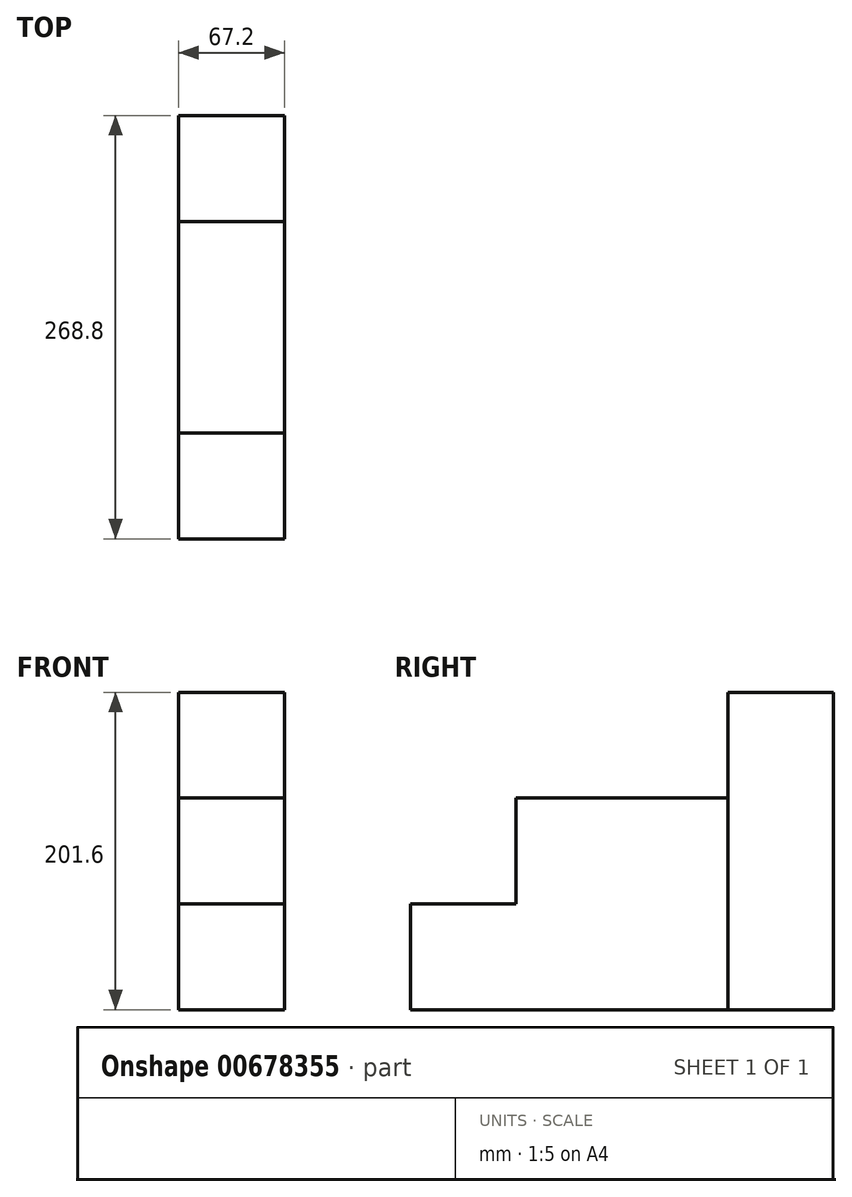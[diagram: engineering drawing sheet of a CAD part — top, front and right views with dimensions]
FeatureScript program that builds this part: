
annotation { "Feature Type Name" : "Feature", "Feature Type Description" : "" }
export const myFeature = defineFeature(function(context is Context, id is Id, definition is map)
    precondition{}
    {
        {
            var Q0;
            Q0=qCreatedBy(makeId("Top.planeOp"),FACE);
            var sketch = newSketch(context, id + "F0", { "sketchPlane" : qUnion([Q0])});
            skLineSegment(sketch, "E0", {"start": v(0, 0) * mm, "end": v(67.2, 0) * mm});
            skLineSegment(sketch, "E1", {"start": v(67.2, 0) * mm, "end": v(67.2, 67.2) * mm});
            skLineSegment(sketch, "E2", {"start": v(67.2, 67.2) * mm, "end": v(0, 67.2) * mm});
            skLineSegment(sketch, "E3", {"start": v(0, 67.2) * mm, "end": v(0, 0) * mm});
            skLineSegment(sketch, "E4.0.1.0", {"start": v(0, 134.4) * mm, "end": v(0, 67.2) * mm});
            skLineSegment(sketch, "E4.0.1.1", {"start": v(0, 67.2) * mm, "end": v(67.2, 67.2) * mm});
            skLineSegment(sketch, "E4.0.1.2", {"start": v(67.2, 67.2) * mm, "end": v(67.2, 134.4) * mm});
            skLineSegment(sketch, "E4.0.1.3", {"start": v(67.2, 134.4) * mm, "end": v(0, 134.4) * mm});
            skLineSegment(sketch, "E4.0.2.0", {"start": v(0, 201.6) * mm, "end": v(0, 134.4) * mm});
            skLineSegment(sketch, "E4.0.2.1", {"start": v(0, 134.4) * mm, "end": v(67.2, 134.4) * mm});
            skLineSegment(sketch, "E4.0.2.2", {"start": v(67.2, 134.4) * mm, "end": v(67.2, 201.6) * mm});
            skLineSegment(sketch, "E4.0.2.3", {"start": v(67.2, 201.6) * mm, "end": v(0, 201.6) * mm});
            skLineSegment(sketch, "E4.0.3.0", {"start": v(0, 268.8) * mm, "end": v(0, 201.6) * mm});
            skLineSegment(sketch, "E4.0.3.1", {"start": v(0, 201.6) * mm, "end": v(67.2, 201.6) * mm});
            skLineSegment(sketch, "E4.0.3.2", {"start": v(67.2, 201.6) * mm, "end": v(67.2, 268.8) * mm});
            skLineSegment(sketch, "E4.0.3.3", {"start": v(67.2, 268.8) * mm, "end": v(0, 268.8) * mm});
            skLineSegment(sketch, "E4.0.4.0", {"start": v(0, 336) * mm, "end": v(0, 268.8) * mm});
            skLineSegment(sketch, "E4.0.4.1", {"start": v(0, 268.8) * mm, "end": v(67.2, 268.8) * mm});
            skLineSegment(sketch, "E4.0.4.2", {"start": v(67.2, 268.8) * mm, "end": v(67.2, 336) * mm});
            skLineSegment(sketch, "E4.0.4.3", {"start": v(67.2, 336) * mm, "end": v(0, 336) * mm});
            skLineSegment(sketch, "E4.1.0.0", {"start": v(67.2, 67.2) * mm, "end": v(67.2, 0) * mm});
            skLineSegment(sketch, "E4.1.0.1", {"start": v(67.2, 0) * mm, "end": v(134.4, 0) * mm});
            skLineSegment(sketch, "E4.1.0.2", {"start": v(134.4, 0) * mm, "end": v(134.4, 67.2) * mm});
            skLineSegment(sketch, "E4.1.0.3", {"start": v(134.4, 67.2) * mm, "end": v(67.2, 67.2) * mm});
            skLineSegment(sketch, "E4.1.1.0", {"start": v(67.2, 134.4) * mm, "end": v(67.2, 67.2) * mm});
            skLineSegment(sketch, "E4.1.1.1", {"start": v(67.2, 67.2) * mm, "end": v(134.4, 67.2) * mm});
            skLineSegment(sketch, "E4.1.1.2", {"start": v(134.4, 67.2) * mm, "end": v(134.4, 134.4) * mm});
            skLineSegment(sketch, "E4.1.1.3", {"start": v(134.4, 134.4) * mm, "end": v(67.2, 134.4) * mm});
            skLineSegment(sketch, "E4.1.2.0", {"start": v(67.2, 201.6) * mm, "end": v(67.2, 134.4) * mm});
            skLineSegment(sketch, "E4.1.2.1", {"start": v(67.2, 134.4) * mm, "end": v(134.4, 134.4) * mm});
            skLineSegment(sketch, "E4.1.2.2", {"start": v(134.4, 134.4) * mm, "end": v(134.4, 201.6) * mm});
            skLineSegment(sketch, "E4.1.2.3", {"start": v(134.4, 201.6) * mm, "end": v(67.2, 201.6) * mm});
            skLineSegment(sketch, "E4.1.3.0", {"start": v(67.2, 268.8) * mm, "end": v(67.2, 201.6) * mm});
            skLineSegment(sketch, "E4.1.3.1", {"start": v(67.2, 201.6) * mm, "end": v(134.4, 201.6) * mm});
            skLineSegment(sketch, "E4.1.3.2", {"start": v(134.4, 201.6) * mm, "end": v(134.4, 268.8) * mm});
            skLineSegment(sketch, "E4.1.3.3", {"start": v(134.4, 268.8) * mm, "end": v(67.2, 268.8) * mm});
            skLineSegment(sketch, "E4.1.4.0", {"start": v(67.2, 336) * mm, "end": v(67.2, 268.8) * mm});
            skLineSegment(sketch, "E4.1.4.1", {"start": v(67.2, 268.8) * mm, "end": v(134.4, 268.8) * mm});
            skLineSegment(sketch, "E4.1.4.2", {"start": v(134.4, 268.8) * mm, "end": v(134.4, 336) * mm});
            skLineSegment(sketch, "E4.1.4.3", {"start": v(134.4, 336) * mm, "end": v(67.2, 336) * mm});
            skLineSegment(sketch, "E4.2.0.0", {"start": v(134.4, 67.2) * mm, "end": v(134.4, 0) * mm});
            skLineSegment(sketch, "E4.2.0.1", {"start": v(134.4, 0) * mm, "end": v(201.6, 0) * mm});
            skLineSegment(sketch, "E4.2.0.2", {"start": v(201.6, 0) * mm, "end": v(201.6, 67.2) * mm});
            skLineSegment(sketch, "E4.2.0.3", {"start": v(201.6, 67.2) * mm, "end": v(134.4, 67.2) * mm});
            skLineSegment(sketch, "E4.2.1.0", {"start": v(134.4, 134.4) * mm, "end": v(134.4, 67.2) * mm});
            skLineSegment(sketch, "E4.2.1.1", {"start": v(134.4, 67.2) * mm, "end": v(201.6, 67.2) * mm});
            skLineSegment(sketch, "E4.2.1.2", {"start": v(201.6, 67.2) * mm, "end": v(201.6, 134.4) * mm});
            skLineSegment(sketch, "E4.2.1.3", {"start": v(201.6, 134.4) * mm, "end": v(134.4, 134.4) * mm});
            skLineSegment(sketch, "E4.2.2.0", {"start": v(134.4, 201.6) * mm, "end": v(134.4, 134.4) * mm});
            skLineSegment(sketch, "E4.2.2.1", {"start": v(134.4, 134.4) * mm, "end": v(201.6, 134.4) * mm});
            skLineSegment(sketch, "E4.2.2.2", {"start": v(201.6, 134.4) * mm, "end": v(201.6, 201.6) * mm});
            skLineSegment(sketch, "E4.2.2.3", {"start": v(201.6, 201.6) * mm, "end": v(134.4, 201.6) * mm});
            skLineSegment(sketch, "E4.2.3.0", {"start": v(134.4, 268.8) * mm, "end": v(134.4, 201.6) * mm});
            skLineSegment(sketch, "E4.2.3.1", {"start": v(134.4, 201.6) * mm, "end": v(201.6, 201.6) * mm});
            skLineSegment(sketch, "E4.2.3.2", {"start": v(201.6, 201.6) * mm, "end": v(201.6, 268.8) * mm});
            skLineSegment(sketch, "E4.2.3.3", {"start": v(201.6, 268.8) * mm, "end": v(134.4, 268.8) * mm});
            skLineSegment(sketch, "E4.2.4.0", {"start": v(134.4, 336) * mm, "end": v(134.4, 268.8) * mm});
            skLineSegment(sketch, "E4.2.4.1", {"start": v(134.4, 268.8) * mm, "end": v(201.6, 268.8) * mm});
            skLineSegment(sketch, "E4.2.4.2", {"start": v(201.6, 268.8) * mm, "end": v(201.6, 336) * mm});
            skLineSegment(sketch, "E4.2.4.3", {"start": v(201.6, 336) * mm, "end": v(134.4, 336) * mm});
            skLineSegment(sketch, "E4.3.0.0", {"start": v(201.6, 67.2) * mm, "end": v(201.6, 0) * mm});
            skLineSegment(sketch, "E4.3.0.1", {"start": v(201.6, 0) * mm, "end": v(268.8, 0) * mm});
            skLineSegment(sketch, "E4.3.0.2", {"start": v(268.8, 0) * mm, "end": v(268.8, 67.2) * mm});
            skLineSegment(sketch, "E4.3.0.3", {"start": v(268.8, 67.2) * mm, "end": v(201.6, 67.2) * mm});
            skLineSegment(sketch, "E4.3.1.0", {"start": v(201.6, 134.4) * mm, "end": v(201.6, 67.2) * mm});
            skLineSegment(sketch, "E4.3.1.1", {"start": v(201.6, 67.2) * mm, "end": v(268.8, 67.2) * mm});
            skLineSegment(sketch, "E4.3.1.2", {"start": v(268.8, 67.2) * mm, "end": v(268.8, 134.4) * mm});
            skLineSegment(sketch, "E4.3.1.3", {"start": v(268.8, 134.4) * mm, "end": v(201.6, 134.4) * mm});
            skLineSegment(sketch, "E4.3.2.0", {"start": v(201.6, 201.6) * mm, "end": v(201.6, 134.4) * mm});
            skLineSegment(sketch, "E4.3.2.1", {"start": v(201.6, 134.4) * mm, "end": v(268.8, 134.4) * mm});
            skLineSegment(sketch, "E4.3.2.2", {"start": v(268.8, 134.4) * mm, "end": v(268.8, 201.6) * mm});
            skLineSegment(sketch, "E4.3.2.3", {"start": v(268.8, 201.6) * mm, "end": v(201.6, 201.6) * mm});
            skLineSegment(sketch, "E4.3.3.0", {"start": v(201.6, 268.8) * mm, "end": v(201.6, 201.6) * mm});
            skLineSegment(sketch, "E4.3.3.1", {"start": v(201.6, 201.6) * mm, "end": v(268.8, 201.6) * mm});
            skLineSegment(sketch, "E4.3.3.2", {"start": v(268.8, 201.6) * mm, "end": v(268.8, 268.8) * mm});
            skLineSegment(sketch, "E4.3.3.3", {"start": v(268.8, 268.8) * mm, "end": v(201.6, 268.8) * mm});
            skLineSegment(sketch, "E4.3.4.0", {"start": v(201.6, 336) * mm, "end": v(201.6, 268.8) * mm});
            skLineSegment(sketch, "E4.3.4.1", {"start": v(201.6, 268.8) * mm, "end": v(268.8, 268.8) * mm});
            skLineSegment(sketch, "E4.3.4.2", {"start": v(268.8, 268.8) * mm, "end": v(268.8, 336) * mm});
            skLineSegment(sketch, "E4.3.4.3", {"start": v(268.8, 336) * mm, "end": v(201.6, 336) * mm});
            skLineSegment(sketch, "E4.4.0.0", {"start": v(268.8, 67.2) * mm, "end": v(268.8, 0) * mm});
            skLineSegment(sketch, "E4.4.0.1", {"start": v(268.8, 0) * mm, "end": v(336, 0) * mm});
            skLineSegment(sketch, "E4.4.0.2", {"start": v(336, 0) * mm, "end": v(336, 67.2) * mm});
            skLineSegment(sketch, "E4.4.0.3", {"start": v(336, 67.2) * mm, "end": v(268.8, 67.2) * mm});
            skLineSegment(sketch, "E4.4.1.0", {"start": v(268.8, 134.4) * mm, "end": v(268.8, 67.2) * mm});
            skLineSegment(sketch, "E4.4.1.1", {"start": v(268.8, 67.2) * mm, "end": v(336, 67.2) * mm});
            skLineSegment(sketch, "E4.4.1.2", {"start": v(336, 67.2) * mm, "end": v(336, 134.4) * mm});
            skLineSegment(sketch, "E4.4.1.3", {"start": v(336, 134.4) * mm, "end": v(268.8, 134.4) * mm});
            skLineSegment(sketch, "E4.4.2.0", {"start": v(268.8, 201.6) * mm, "end": v(268.8, 134.4) * mm});
            skLineSegment(sketch, "E4.4.2.1", {"start": v(268.8, 134.4) * mm, "end": v(336, 134.4) * mm});
            skLineSegment(sketch, "E4.4.2.2", {"start": v(336, 134.4) * mm, "end": v(336, 201.6) * mm});
            skLineSegment(sketch, "E4.4.2.3", {"start": v(336, 201.6) * mm, "end": v(268.8, 201.6) * mm});
            skLineSegment(sketch, "E4.4.3.0", {"start": v(268.8, 268.8) * mm, "end": v(268.8, 201.6) * mm});
            skLineSegment(sketch, "E4.4.3.1", {"start": v(268.8, 201.6) * mm, "end": v(336, 201.6) * mm});
            skLineSegment(sketch, "E4.4.3.2", {"start": v(336, 201.6) * mm, "end": v(336, 268.8) * mm});
            skLineSegment(sketch, "E4.4.3.3", {"start": v(336, 268.8) * mm, "end": v(268.8, 268.8) * mm});
            skLineSegment(sketch, "E4.4.4.0", {"start": v(268.8, 336) * mm, "end": v(268.8, 268.8) * mm});
            skLineSegment(sketch, "E4.4.4.1", {"start": v(268.8, 268.8) * mm, "end": v(336, 268.8) * mm});
            skLineSegment(sketch, "E4.4.4.2", {"start": v(336, 268.8) * mm, "end": v(336, 336) * mm});
            skLineSegment(sketch, "E4.4.4.3", {"start": v(336, 336) * mm, "end": v(268.8, 336) * mm});
            skLineSegment(sketch, "E4.direction1", {"start": v(0, 0) * mm, "end": v(67.2, 0) * mm, "construction": true});
            skLineSegment(sketch, "E4.direction2", {"start": v(0, 0) * mm, "end": v(0, 67.2) * mm, "construction": true});
            skSolve(sketch);
        }
        {
            var Q0;
            Q0=makeQuery(id+"F0.imprint","IMPRINT",FACE,{"disambiguationData":[TD([[makeQuery(id+"F0.imprint","IMPRINT",EDGE,{"derivedFrom":sQuery(id+"F0.wireOp",EDGE,"E4.0.4.0")}),1.0]])]});
            var Q1;
            Q1=makeQuery(id+"F0.imprint","IMPRINT",FACE,{"disambiguationData":[TD([[makeQuery(id+"F0.imprint","IMPRINT",EDGE,{"derivedFrom":sQuery(id+"F0.wireOp",EDGE,"E4.4.4.0")}),1.0]])]});
            var Q2;
            Q2=makeQuery(id+"F0.imprint","IMPRINT",FACE,{"disambiguationData":[TD([[makeQuery(id+"F0.imprint","IMPRINT",EDGE,{"derivedFrom":sQuery(id+"F0.wireOp",EDGE,"E4.4.3.0")}),1.0]])]});
            var Q3;
            Q3=makeQuery(id+"F0.imprint","IMPRINT",FACE,{"disambiguationData":[TD([[makeQuery(id+"F0.imprint","IMPRINT",EDGE,{"derivedFrom":sQuery(id+"F0.wireOp",EDGE,"E4.1.4.0")}),1.0]])]});
            var Q4;
            Q4=makeQuery(id+"F0.imprint","IMPRINT",FACE,{"disambiguationData":[TD([[makeQuery(id+"F0.imprint","IMPRINT",EDGE,{"derivedFrom":sQuery(id+"F0.wireOp",EDGE,"E4.3.4.0")}),1.0]])]});
            extrude(context, id + "F1", {"entities" : qUnion([Q0, Q1, Q2, Q3, Q4]), "depth" : (336 * 3 / 5) * mm, "offsetDistance" : 25 * mm});
        }
        {
            var Q0;
            Q0=makeQuery(id+"F0.imprint","IMPRINT",FACE,{"disambiguationData":[TD([[makeQuery(id+"F0.imprint","IMPRINT",EDGE,{"derivedFrom":sQuery(id+"F0.wireOp",EDGE,"E4.0.3.0")}),1.0]])]});
            var Q1;
            Q1=makeQuery(id+"F0.imprint","IMPRINT",FACE,{"disambiguationData":[TD([[makeQuery(id+"F0.imprint","IMPRINT",EDGE,{"derivedFrom":sQuery(id+"F0.wireOp",EDGE,"E4.0.2.0")}),1.0]])]});
            var Q2;
            Q2=makeQuery(id+"F0.imprint","IMPRINT",FACE,{"disambiguationData":[TD([[makeQuery(id+"F0.imprint","IMPRINT",EDGE,{"derivedFrom":sQuery(id+"F0.wireOp",EDGE,"E4.3.3.0")}),1.0]])]});
            var Q3;
            Q3=makeQuery(id+"F0.imprint","IMPRINT",FACE,{"disambiguationData":[TD([[makeQuery(id+"F0.imprint","IMPRINT",EDGE,{"derivedFrom":sQuery(id+"F0.wireOp",EDGE,"E4.4.2.0")}),1.0]])]});
            var Q4;
            Q4=makeQuery(id+"F0.imprint","IMPRINT",FACE,{"disambiguationData":[TD([[makeQuery(id+"F0.imprint","IMPRINT",EDGE,{"derivedFrom":sQuery(id+"F0.wireOp",EDGE,"E4.2.4.0")}),1.0]])]});
            extrude(context, id + "F2", {"entities" : qUnion([Q0, Q1, Q2, Q3, Q4]), "depth" : (336 * 2 / 5) * mm, "offsetDistance" : 25 * mm});
        }
        {
            var Q0;
            Q0=makeQuery(id+"F0.imprint","IMPRINT",FACE,{"disambiguationData":[TD([[makeQuery(id+"F0.imprint","IMPRINT",EDGE,{"derivedFrom":sQuery(id+"F0.wireOp",EDGE,"E4.1.2.0")}),1.0]])]});
            var Q1;
            Q1=makeQuery(id+"F0.imprint","IMPRINT",FACE,{"disambiguationData":[TD([[makeQuery(id+"F0.imprint","IMPRINT",EDGE,{"derivedFrom":sQuery(id+"F0.wireOp",EDGE,"E4.0.1.0")}),1.0]])]});
            var Q2;
            Q2=makeQuery(id+"F0.imprint","IMPRINT",FACE,{"disambiguationData":[TD([[makeQuery(id+"F0.imprint","IMPRINT",EDGE,{"derivedFrom":sQuery(id+"F0.wireOp",EDGE,"E4.3.1.0")}),1.0]])]});
            var Q3;
            Q3=makeQuery(id+"F0.imprint","IMPRINT",FACE,{"disambiguationData":[TD([[makeQuery(id+"F0.imprint","IMPRINT",EDGE,{"derivedFrom":sQuery(id+"F0.wireOp",EDGE,"E4.4.1.0")}),1.0]])]});
            var Q4;
            Q4=makeQuery(id+"F0.imprint","IMPRINT",FACE,{"disambiguationData":[TD([[makeQuery(id+"F0.imprint","IMPRINT",EDGE,{"derivedFrom":sQuery(id+"F0.wireOp",EDGE,"E4.3.2.0")}),1.0]])]});
            var Q5;
            Q5=makeQuery(id+"F0.imprint","IMPRINT",FACE,{"disambiguationData":[TD([[makeQuery(id+"F0.imprint","IMPRINT",EDGE,{"derivedFrom":sQuery(id+"F0.wireOp",EDGE,"E4.1.3.0")}),1.0]])]});
            var Q6;
            Q6=makeQuery(id+"F0.imprint","IMPRINT",FACE,{"disambiguationData":[TD([[makeQuery(id+"F0.imprint","IMPRINT",EDGE,{"derivedFrom":sQuery(id+"F0.wireOp",EDGE,"E4.2.3.0")}),1.0]])]});
            var Q7;
            Q7=makeQuery(id+"F0.imprint","IMPRINT",FACE,{"disambiguationData":[TD([[makeQuery(id+"F0.imprint","IMPRINT",EDGE,{"derivedFrom":sQuery(id+"F0.wireOp",EDGE,"E4.4.0.0")}),1.0]])]});
            extrude(context, id + "F3", {"entities" : qUnion([Q0, Q1, Q2, Q3, Q4, Q5, Q6, Q7]), "operationType" : NewBodyOperationType.ADD, "depth" : 336 / 5 * mm, "offsetDistance" : 25 * mm});
        }
    });
